# Revit family: Clarus_Go Mobile_R20
name_source: partatom
category: Furniture
units: mm (PartAtom-declared; Revit-internal decimal feet)

## family parameters
Cut with Voids When Loaded = No
Host = Face
Room Calculation Point = No
Shared = No

## types (7) — shared parameters
Caster Wheel = Clarus Black
Default Elevation = 0"
Depth = 21"
Description = The glassboard goes mobile. Take a look at our most popular product and how it's transforming everyday spaces into collaborative hotspots.
Extension = 2 21/32"
Manufacturer = Clarus
Model = go Mobile
Modeled By = Commense Studio
Product URL = https://www.clarus.com
URL = https://www.clarus.com

## per-type parameters (varying)
| type | 3 Wheel | 4 wheel | Height | Width |
| Four Wheel XS (40" X 54") | No | Yes | 54" | 40" |
| Four Wheel S (60″ x 54″) | No | Yes | 54" | 60" |
| Four Wheel M (40″ x 73″) | No | Yes | 73" | 40" |
| Four Wheel XL (60″ x 73″) | No | Yes | 73" | 60" |
| Three Wheel XS (40″ x 54″) | Yes | No | 54" | 40" |
| Three Wheel S (60″ x 54″) | Yes | No | 54" | 60" |
| Three Wheel M (40″ x 73″) | Yes | No | 73" | 40" |

## geometry (parser evidence)
native form markers: Sweep x4
no freeform markers — native parametric forms only
